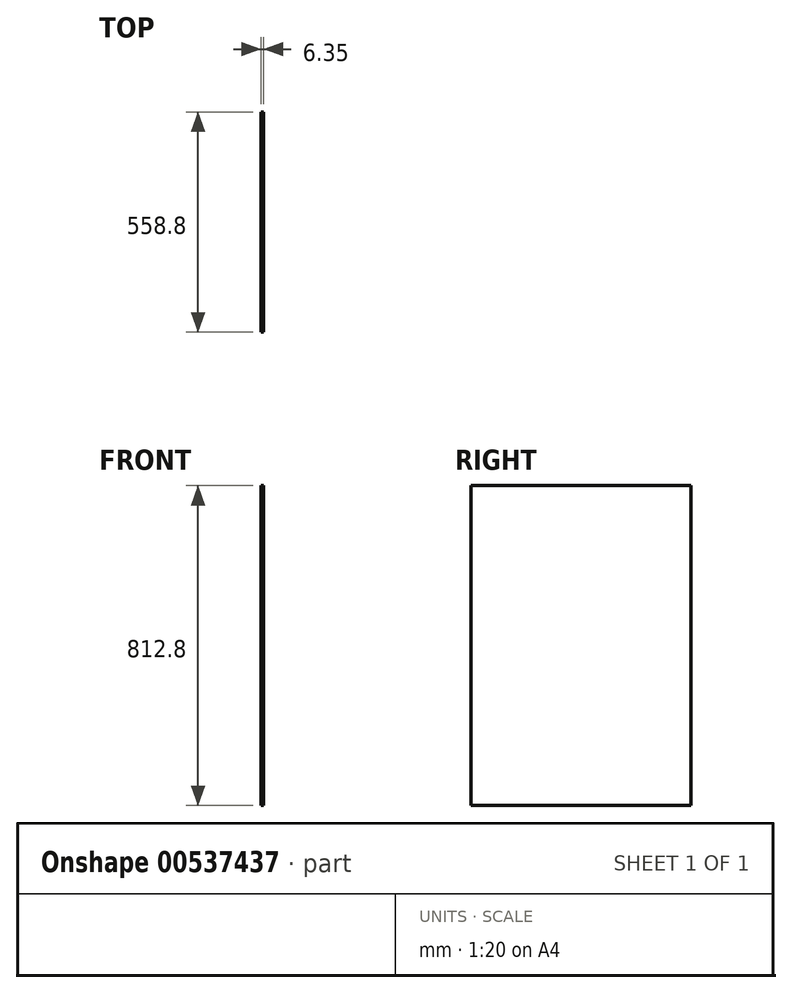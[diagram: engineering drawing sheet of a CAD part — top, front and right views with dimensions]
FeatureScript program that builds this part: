
annotation { "Feature Type Name" : "Feature", "Feature Type Description" : "" }
export const myFeature = defineFeature(function(context is Context, id is Id, definition is map)
    precondition{}
    {
        {
            var Q0;
            Q0=qCreatedBy(makeId("Right.planeOp"),FACE);
            var sketch = newSketch(context, id + "F0", { "sketchPlane" : qUnion([Q0])});
            skLineSegment(sketch, "E0.bottom", {"start": v(279.4, 406.4) * mm, "end": v(-279.4, 406.4) * mm});
            skLineSegment(sketch, "E0.top", {"start": v(279.4, -406.4) * mm, "end": v(-279.4, -406.4) * mm});
            skLineSegment(sketch, "E0.left", {"start": v(279.4, 406.4) * mm, "end": v(279.4, -406.4) * mm});
            skLineSegment(sketch, "E0.right", {"start": v(-279.4, 406.4) * mm, "end": v(-279.4, -406.4) * mm});
            skPoint(sketch, "E0.middle", {"position": v(0, 0) * mm});
            skSolve(sketch);
        }
        {
            var Q0;
            Q0 = qSketchRegion(id + "F0", true);
            extrude(context, id + "F1", {"entities" : qUnion([Q0]), "depth" : 6.35 * mm, "offsetDistance" : 25.4 * mm});
        }
    });
